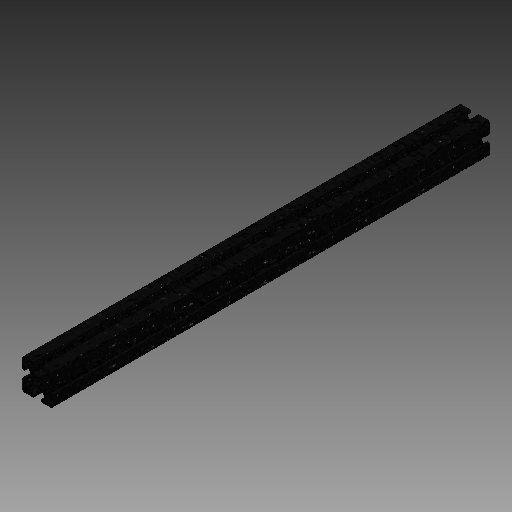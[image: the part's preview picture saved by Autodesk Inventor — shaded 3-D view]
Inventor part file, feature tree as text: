
AUTODESK INVENTOR PART (.ipt)
format: ipt  version: 2019 (Build 230136000, 136)  size: 258,048 bytes
history: native  units: in
note: dims shown in document units (in); Inventor stores cm internally (conversion verified against a paired STEP export)
features: plane x1, extrude x1, sketch x1
ambient origin geometry x8: Origin, YZ Plane, XZ Plane, XY Plane, X Axis, Y Axis, Z Axis, Center Point
bodies: Solid1 (feature_tree)
feature tree (3):
  plane  "Work Plane1"
  extrude  "Extrusion1"  [1 undecoded]
  sketch  "Sketch1"  dims[d0=21.0in d1=0.0in]
note: 1 required parameter value undecoded (feature->parameter linkage not recoverable at this tier; creation-order binding heuristic only, values carry confidence <= 0.55)
